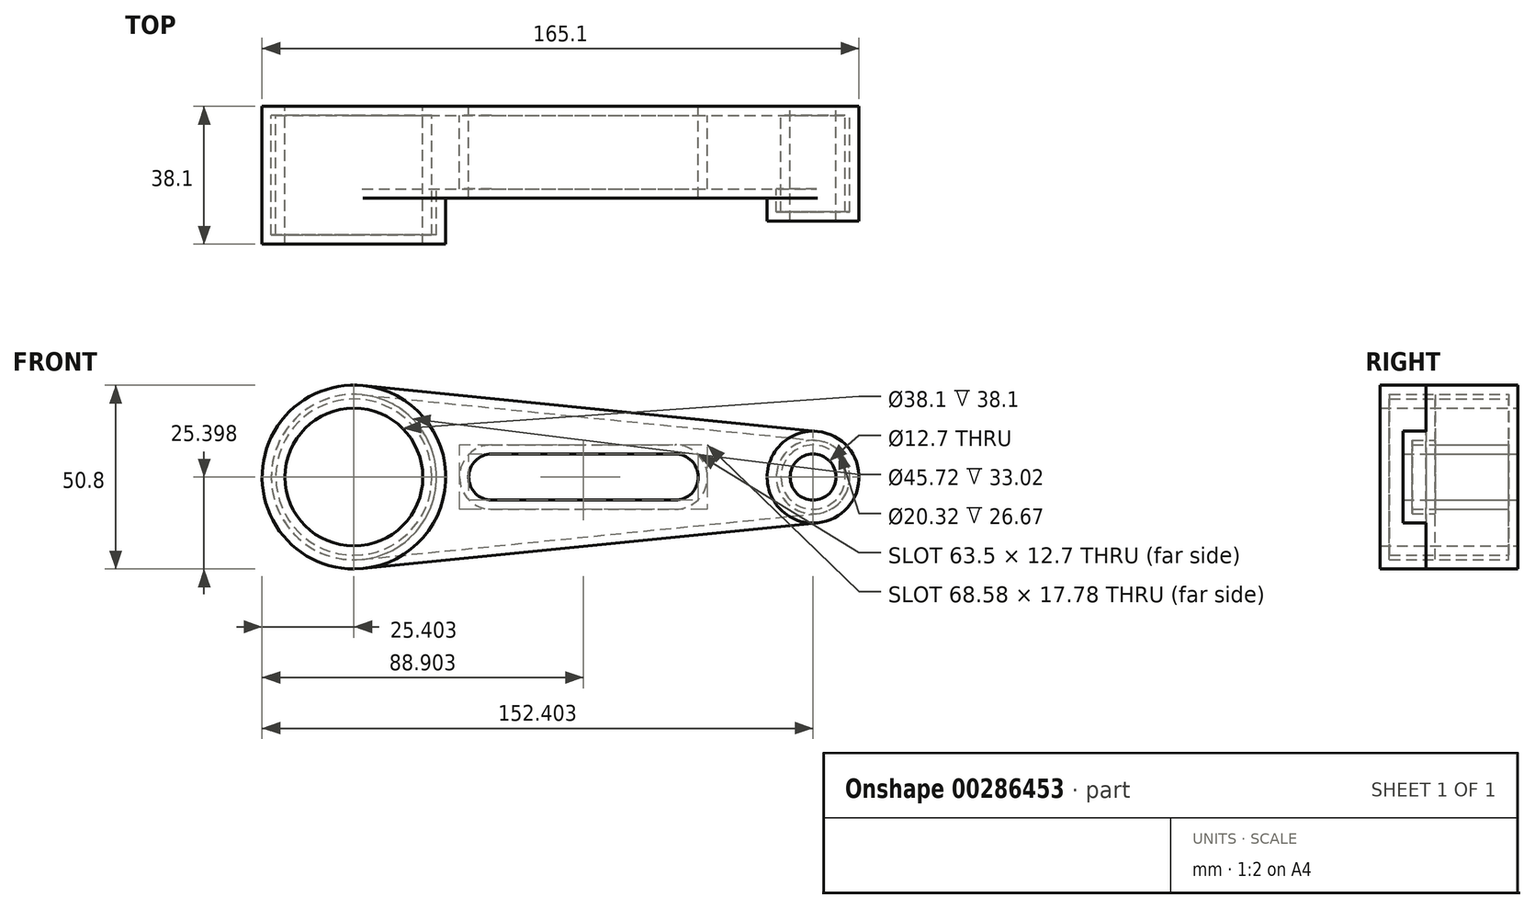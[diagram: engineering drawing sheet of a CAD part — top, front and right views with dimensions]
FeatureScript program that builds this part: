
annotation { "Feature Type Name" : "Feature", "Feature Type Description" : "" }
export const myFeature = defineFeature(function(context is Context, id is Id, definition is map)
    precondition{}
    {
        {
            var Q0;
            Q0=qCreatedBy(makeId("Front.planeOp"),FACE);
            var sketch = newSketch(context, id + "F0", { "sketchPlane" : qUnion([Q0])});
            skCircle(sketch, "E0", {"center": v(-104.56, 126.54) * mm, "radius": 25.4 * mm});
            skCircle(sketch, "E1", {"center": v(22.44, 126.54) * mm, "radius": 12.7 * mm});
            skArc(sketch, "E2", {"start": v(-66.46, 132.89) * mm, "mid": v(-72.8, 126.54) * mm, "end": v(-66.46, 120.19) * mm});
            skArc(sketch, "E3", {"start": v(-15.66, 120.19) * mm, "mid": v(-9.3, 126.54) * mm, "end": v(-15.66, 132.89) * mm});
            skCircle(sketch, "E4", {"center": v(-104.56, 126.54) * mm, "radius": 19.05 * mm});
            skCircle(sketch, "E5", {"center": v(22.44, 126.54) * mm, "radius": 6.35 * mm});
            skLineSegment(sketch, "E6", {"start": v(-102.02, 101.27) * mm, "end": v(23.71, 113.9) * mm});
            skLineSegment(sketch, "E7", {"start": v(-102.02, 151.81) * mm, "end": v(23.71, 139.17) * mm});
            skLineSegment(sketch, "E8", {"start": v(-87.03, 132.89) * mm, "end": v(-86.6, 132.89) * mm});
            skLineSegment(sketch, "E9.trimOffspring", {"start": v(-66.46, 120.19) * mm, "end": v(-15.66, 120.19) * mm});
            skLineSegment(sketch, "E10.trimOffspring", {"start": v(-66.46, 132.89) * mm, "end": v(-15.66, 132.89) * mm});
            skLineSegment(sketch, "E11", {"start": v(-98.35, 85.6) * mm, "end": v(-42.42, 76.96) * mm});
            skLineSegment(sketch, "E12.bottom", {"start": v(-154.85, 103.29) * mm, "end": v(-136.8, 103.29) * mm});
            skLineSegment(sketch, "E12.top", {"start": v(-154.85, 83.5) * mm, "end": v(-124.1, 83.5) * mm});
            skLineSegment(sketch, "E12.left", {"start": v(-154.85, 103.29) * mm, "end": v(-154.85, 83.5) * mm});
            skLineSegment(sketch, "E12.right", {"start": v(-124.1, 90.59) * mm, "end": v(-124.1, 83.5) * mm});
            skCircle(sketch, "E13", {"center": v(-49.72, 89.26) * mm, "radius": 8.56 * mm});
            skArc(sketch, "E14", {"start": v(16.58, 85.03) * mm, "mid": v(3.3, 89.34) * mm, "end": v(-9.55, 83.88) * mm});
            skPoint(sketch, "E15.visualSharp", {"position": v(-124.1, 103.29) * mm});
            skArc(sketch, "E15.filletArc", {"start": v(-124.1, 90.59) * mm, "mid": v(-127.82, 99.57) * mm, "end": v(-136.8, 103.29) * mm});
            skLineSegment(sketch, "E16.0", {"start": v(-130.45, 90.59) * mm, "end": v(-130.45, 83.5) * mm});
            skArc(sketch, "E16.1", {"start": v(-130.45, 90.59) * mm, "mid": v(-132.3, 95.08) * mm, "end": v(-136.8, 96.94) * mm});
            skLineSegment(sketch, "E16.2", {"start": v(-154.85, 96.94) * mm, "end": v(-136.8, 96.94) * mm});
            skLineSegment(sketch, "E17.0", {"start": v(-161.2, 77.14) * mm, "end": v(-124.1, 77.14) * mm});
            skLineSegment(sketch, "E17.1", {"start": v(-161.2, 103.29) * mm, "end": v(-161.2, 77.14) * mm});
            skSolve(sketch);
        }
        {
            var Q0;
            Q0=makeQuery(id+"F0.imprint","IMPRINT",FACE,{"disambiguationData":[TD([[makeQuery(id+"F0.imprint","IMPRINT",EDGE,{"derivedFrom":sQuery(id+"F0.wireOp",EDGE,"E4")}),-1.0]])]});
            extrude(context, id + "F1", {"entities" : qUnion([Q0]), "depth" : 38.1 * mm});
        }
        {
            var Q0;
            Q0=makeQuery(id+"F0.imprint","IMPRINT",FACE,{"disambiguationData":[TD([[makeQuery(id+"F0.imprint","IMPRINT",EDGE,{"derivedFrom":sQuery(id+"F0.wireOp",EDGE,"E2")}),-1.0]])]});
            extrude(context, id + "F2", {"entities" : qUnion([Q0]), "operationType" : NewBodyOperationType.ADD, "depth" : 25.4 * mm});
        }
        {
            var Q0;
            Q0=makeQuery(id+"F0.imprint","IMPRINT",FACE,{"disambiguationData":[TD([[makeQuery(id+"F0.imprint","IMPRINT",EDGE,{"derivedFrom":sQuery(id+"F0.wireOp",EDGE,"E5")}),-1.0]])]});
            extrude(context, id + "F3", {"entities" : qUnion([Q0]), "operationType" : NewBodyOperationType.ADD, "depth" : 31.75 * mm});
        }
        {
            var Q0;
            Q0=makeQuery(id+"F2.opExtrude","CAP_FACE",FACE,{"disambiguationData":[OSD([sQuery(id+"F0.wireOp",EDGE,"E0"),sQuery(id+"F0.wireOp",EDGE,"E1"),sQuery(id+"F0.wireOp",EDGE,"E2"),sQuery(id+"F0.wireOp",EDGE,"E3"),sQuery(id+"F0.wireOp",EDGE,"E6"),sQuery(id+"F0.wireOp",EDGE,"E7"),sQuery(id+"F0.wireOp",EDGE,"E9.trimOffspring"),sQuery(id+"F0.wireOp",EDGE,"E10.trimOffspring")])],"isStart":false});
            var Q1;
            Q1=makeQuery(id+"F1.opExtrude","CAP_FACE",FACE,{"disambiguationData":[OSD([sQuery(id+"F0.wireOp",EDGE,"E0"),sQuery(id+"F0.wireOp",EDGE,"E4")])],"isStart":false});
            var Q2;
            Q2=makeQuery(id+"F3.opExtrude","CAP_FACE",FACE,{"disambiguationData":[OSD([sQuery(id+"F0.wireOp",EDGE,"E1"),sQuery(id+"F0.wireOp",EDGE,"E5")])],"isStart":false});
            var Q3;
            Q3=makeQuery(id+"F1.opExtrude","SWEPT_BODY",BODY,{"disambiguationData":[OSD([sQuery(id+"F0.wireOp",EDGE,"E0"),sQuery(id+"F0.wireOp",EDGE,"E4")])]});
            shell(context, id + "F4", {"isHollow" : true, "entities" : qUnion([Q0, Q1, Q2]), "parts" : qUnion([Q3]), "thickness" : 2.54 * mm});
        }
    });
